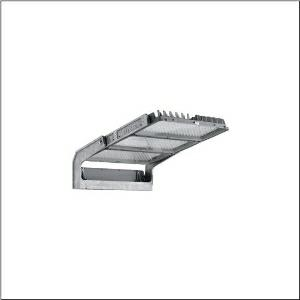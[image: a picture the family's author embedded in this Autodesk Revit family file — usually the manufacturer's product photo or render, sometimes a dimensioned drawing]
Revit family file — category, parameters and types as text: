
# Revit family: floodlight_fl_11_maxi_pro___rs08_5xa779128l01gb_a40c
name_source: partatom
category: Lighting Fixtures
units: mm (PartAtom-declared; Revit-internal decimal feet)

## family parameters
Cut with Voids When Loaded = No
Host = Face
Light Source = No
Part Type = Normal
Room Calculation Point = No
Round Connector Dimension = Use Diameter
Shared = No

## types (1)
- --- (1 x LED, 148170 lm, 1285.1 W, 5700K)
    Apparent Load = 1285 VA
    CIE Flux Codes = 70 87 98 100 100
    Color Rendering = 80
    Color Temperature = 5700K
    Default Elevation = 1800 mm
    Description = Floodlight FL 11  maxi  pro floodlight; light control with lens of PMMA; cover panel of toughened safety glass, transparent; light distribution: RS08, rotationally symmetric direct distribution, LEDcolour temperature: 5700K, rated luminous flux: 148.170lm, colour rendering: CRI > 80, light colour: 857; luminous efficacy: 115lm/W; brightness control: DALI 2; with terminal, 5-pole, max. 2.5mm², mains connection: 220..240V/380..400V AC, 50/60Hz, surge voltage resistance: line to ground: 10kV, service life up to 100,000h L90. Typical operating time: 1000h per year, ECG replaceable separately, LED unit replaceable without ESD environment, dustproof LED module, dimming range 10..100%; 1285W floodlight with 3x LED unit of diecast aluminium, coated grey; length: 1.003mm / width: 651mm / height: 338mm; mounting bracket, of diecast aluminium, uncoated, natural, protection rating (complete): IP66; insulation class (complete): insulation class I (protective earthing); certification: CE, ENEC, VDE; ball protection: ball impact resistant, only for outdoor installations in the designated locations, permissible operating ambient temperature: -45..+55°C, permissible storage temperature: -40..+85°Cpackaging unit: 1 piece

Light Distribution: RS08
    Height = 320 mm
    Lamp = 1 x LED
    Lamp Light Flux = 148170 lm
    Lamp Power = 1285.1 W
    Lamp count = 1
    Length = 1002 mm
    Luminous efficacy = 115 lm/W
    Manufacturer = Siteco
    ModVariant = No
    Model = 5XA779128L01GB
    Mounting Place = Ceiling
    Mounting Type = Surface mounted
    Number of Poles = 1
    OnlyDefault = Yes
    Power Factor = 1
    Product Name = Floodlight FL 11 maxi pro | RS08
    Product group = floodlight | ceiling mounted
    ProductGroupID = 301
    Protection Class = Protection class I
    Protection Degree = IP 66
    RLX_Detail_Level = 1
    RLX_Emergency_Light_Flux = 0 lm
    RLX_Emergency_Type = 0
    RLX_Emergency_Type_DB = No
    RlxData = <blob elided: 40181 chars, md5=aa57f097>
    Socket = socket
    Standby Power = 0 W
    System Light Flux = 148170 lm
    System Power = 1285 W
    Type Comments = factory setting: luminous flux: 100 % | dim-lin: 254 | 875 mA
    Type Image = l_1356210.jpg
    URL = http://relux.com
    VarID = @adj_024886
    Voltage = 0 V
    Weight = 0.00 kg
    Width = 655 mm

## geometry (parser evidence)
native form markers: Blend x4, Sweep x16
no freeform markers — native parametric forms only
